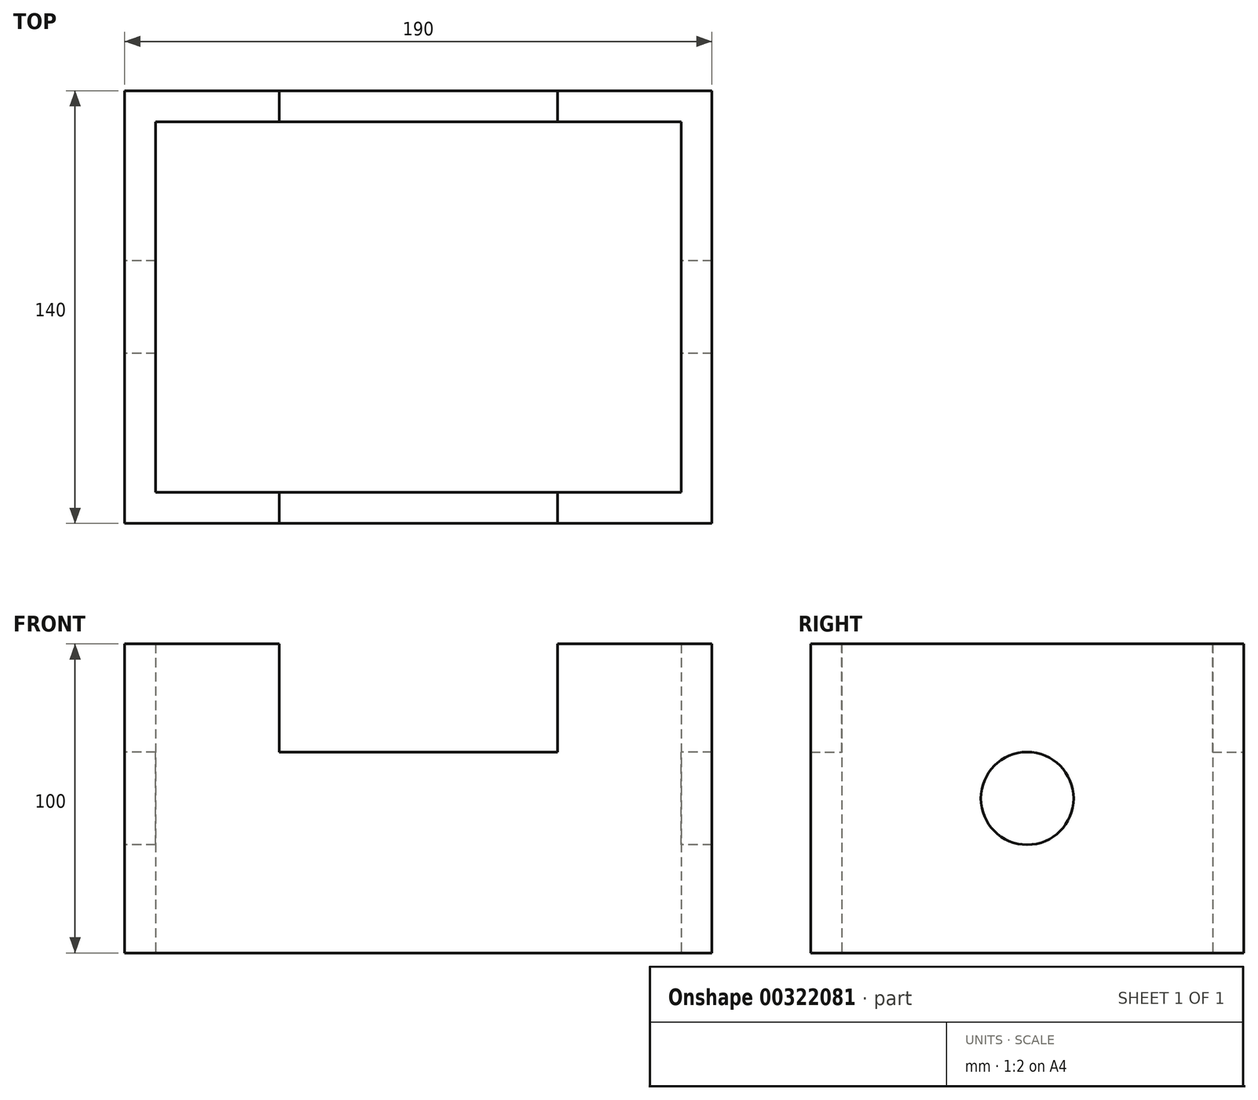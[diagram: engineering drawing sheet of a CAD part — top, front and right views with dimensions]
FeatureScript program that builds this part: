
annotation { "Feature Type Name" : "Feature", "Feature Type Description" : "" }
export const myFeature = defineFeature(function(context is Context, id is Id, definition is map)
    precondition{}
    {
        {
            var Q0;
            Q0=qCreatedBy(makeId("Top.planeOp"),FACE);
            var sketch = newSketch(context, id + "F0", { "sketchPlane" : qUnion([Q0])});
            skLineSegment(sketch, "E0.bottom", {"start": v(-85, 60) * mm, "end": v(85, 60) * mm});
            skLineSegment(sketch, "E0.top", {"start": v(-85, -60) * mm, "end": v(85, -60) * mm});
            skLineSegment(sketch, "E0.left", {"start": v(-85, 60) * mm, "end": v(-85, -60) * mm});
            skLineSegment(sketch, "E0.right", {"start": v(85, 60) * mm, "end": v(85, -60) * mm});
            skPoint(sketch, "E0.middle", {"position": v(0, 0) * mm});
            skLineSegment(sketch, "E1.bottom", {"start": v(-95, 70) * mm, "end": v(95, 70) * mm});
            skLineSegment(sketch, "E1.top", {"start": v(-95, -70) * mm, "end": v(95, -70) * mm});
            skLineSegment(sketch, "E1.left", {"start": v(-95, 70) * mm, "end": v(-95, -70) * mm});
            skLineSegment(sketch, "E1.right", {"start": v(95, 70) * mm, "end": v(95, -70) * mm});
            skSolve(sketch);
        }
        {
            var Q0;
            Q0=makeQuery(id+"F0.imprint","IMPRINT",FACE,{"disambiguationData":[TD([[makeQuery(id+"F0.imprint","IMPRINT",EDGE,{"derivedFrom":sQuery(id+"F0.wireOp",EDGE,"E0.bottom")}),1.0]])]});
            extrude(context, id + "F1", {"entities" : qUnion([Q0]), "depth" : 100 * mm});
        }
        {
            var Q0;
            Q0=makeQuery(id+"F1.opExtrude","SWEPT_FACE",FACE,{"disambiguationData":[OSD([sQuery(id+"F0.wireOp",EDGE,"E1.left")])]});
            var sketch = newSketch(context, id + "F2", { "sketchPlane" : qUnion([Q0])});
            skCircle(sketch, "E2", {"center": v(0, 50) * mm, "radius": 15 * mm});
            skPoint(sketch, "E2.centerSnap0", {"position": v(-70, 50) * mm});
            skPoint(sketch, "E2.centerSnap1", {"position": v(0, 100) * mm});
            skSolve(sketch);
        }
        {
            var Q0;
            Q0=makeQuery(id+"F2.imprint","IMPRINT",FACE,{"disambiguationData":[TD([[makeQuery(id+"F2.imprint","IMPRINT",EDGE,{"derivedFrom":sQuery(id+"F2.wireOp",EDGE,"E2")}),1.0]])]});
            var Q1;
            Q1=makeQuery(id+"F1.opExtrude","SWEPT_FACE",FACE,{"disambiguationData":[OSD([sQuery(id+"F0.wireOp",EDGE,"E1.right")])]});
            extrude(context, id + "F3", {"entities" : qUnion([Q0]), "operationType" : NewBodyOperationType.REMOVE, "endBound" : BoundingType.UP_TO_SURFACE, "oppositeDirection" : true, "endBoundEntityFace" : qUnion([Q1]), "depth" : 25 * mm});
        }
        {
            var Q0;
            Q0=makeQuery(id+"F1.opExtrude","SWEPT_FACE",FACE,{"disambiguationData":[OSD([sQuery(id+"F0.wireOp",EDGE,"E1.bottom")])]});
            var sketch = newSketch(context, id + "F4", { "sketchPlane" : qUnion([Q0])});
            skLineSegment(sketch, "E3.bottom", {"start": v(45, 65) * mm, "end": v(-45, 65) * mm});
            skLineSegment(sketch, "E3.top", {"start": v(45, 135) * mm, "end": v(-45, 135) * mm});
            skLineSegment(sketch, "E3.left", {"start": v(45, 65) * mm, "end": v(45, 135) * mm});
            skLineSegment(sketch, "E3.right", {"start": v(-45, 65) * mm, "end": v(-45, 135) * mm});
            skPoint(sketch, "E3.middle", {"position": v(0, 100) * mm});
            skSolve(sketch);
        }
        {
            var Q0;
            {var subQ0=sQuery(id+"F4.wireOp",EDGE,"E3.bottom");Q0=makeQuery(id+"F4.imprint","IMPRINT",FACE,{"disambiguationData":[TD([[makeQuery(id+"F4.imprint","IMPRINT",EDGE,{"derivedFrom":subQ0}),-1.0]])]});}
            var Q1;
            Q1=makeQuery(id+"F1.opExtrude","SWEPT_FACE",FACE,{"disambiguationData":[OSD([sQuery(id+"F0.wireOp",EDGE,"E1.top")])]});
            extrude(context, id + "F5", {"entities" : qUnion([Q0]), "operationType" : NewBodyOperationType.REMOVE, "endBound" : BoundingType.UP_TO_SURFACE, "oppositeDirection" : true, "endBoundEntityFace" : qUnion([Q1]), "depth" : 25 * mm});
        }
    });
